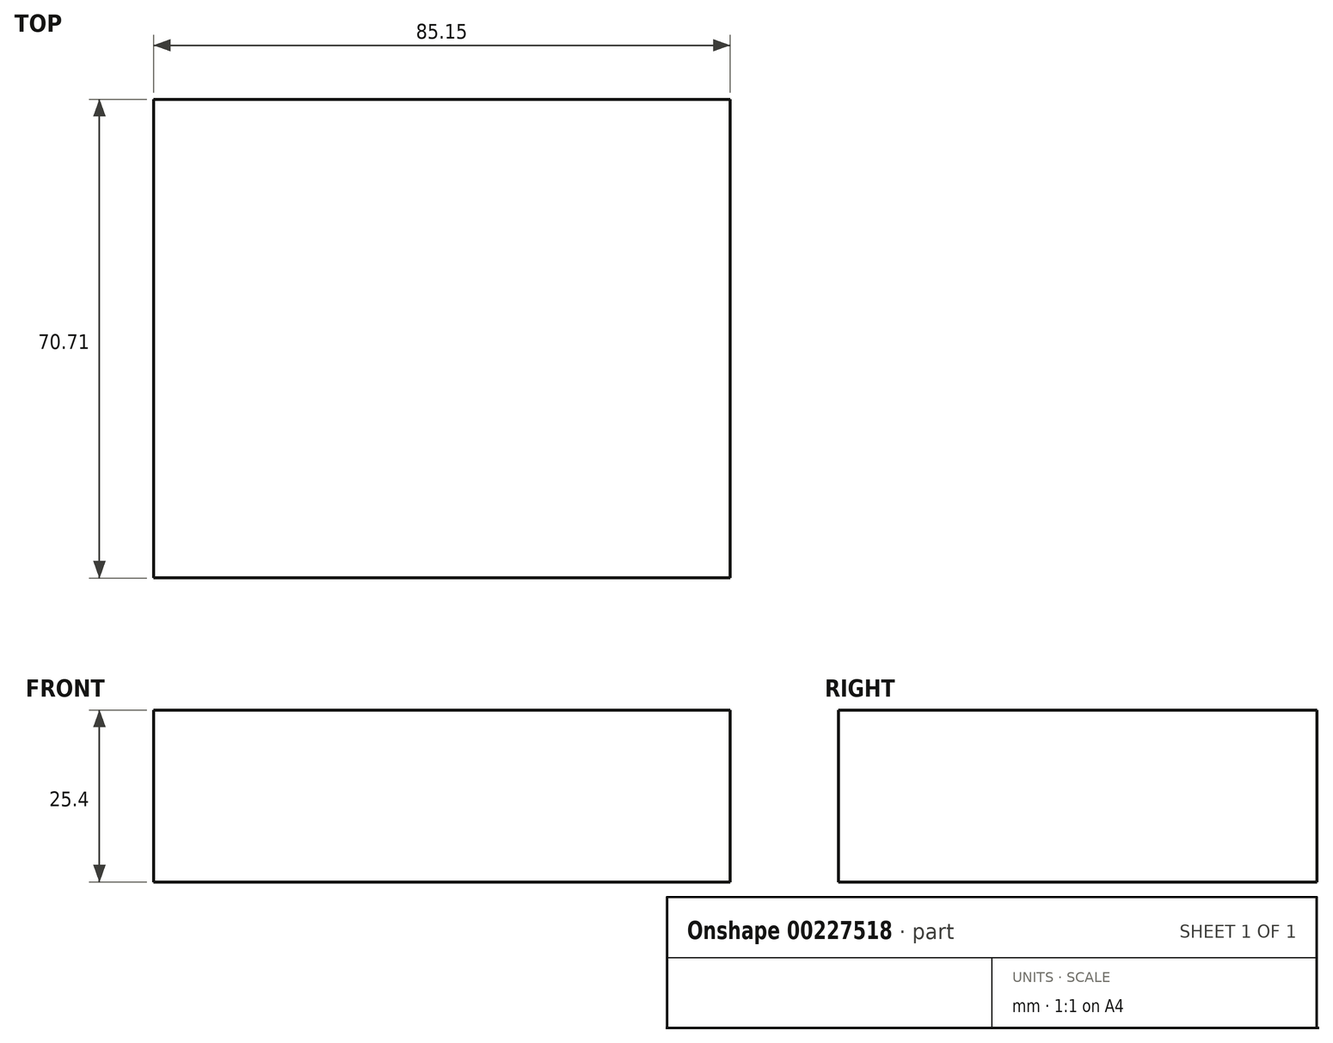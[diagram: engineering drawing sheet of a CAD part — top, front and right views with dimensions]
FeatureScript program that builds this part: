
annotation { "Feature Type Name" : "Feature", "Feature Type Description" : "" }
export const myFeature = defineFeature(function(context is Context, id is Id, definition is map)
    precondition{}
    {
        {
            var Q0;
            Q0=qCreatedBy(makeId("Top.planeOp"),FACE);
            var sketch = newSketch(context, id + "F0", { "sketchPlane" : qUnion([Q0])});
            skLineSegment(sketch, "E0.bottom", {"start": v(-43.47, -35.22) * mm, "end": v(41.68, -35.22) * mm});
            skLineSegment(sketch, "E0.top", {"start": v(-43.47, 35.49) * mm, "end": v(41.68, 35.49) * mm});
            skLineSegment(sketch, "E0.left", {"start": v(-43.47, -35.22) * mm, "end": v(-43.47, 35.49) * mm});
            skLineSegment(sketch, "E0.right", {"start": v(41.68, -35.22) * mm, "end": v(41.68, 35.49) * mm});
            skSolve(sketch);
        }
        {
            var Q0;
            Q0 = qSketchRegion(id + "F0", true);
            extrude(context, id + "F1", {"entities" : qUnion([Q0]), "depth" : 25.4 * mm});
        }
    });
